# Revit family: 2019-SYP-ALTAIR-120-RE-EN
name_source: partatom
category: Mechanical Equipment
units: mm (PartAtom-declared; Revit-internal decimal feet)

## family parameters
Always vertical = Yes
Cut with Voids When Loaded = No
OmniClass Number = 23.75.00.00
OmniClass Title = Climate Control (HVAC)
Part Type = Normal
Room Calculation Point = No
Round Connector Dimension = Use Radius
Shared = No
Work Plane-Based = No

## types (1)
- default
    Air Terminal Velocity Pressure = 0.0 Pa
    AtmosphericAcidification = 0
    AtmosphericAcidificationPerUnit = 0
    BIMElementVersion = 1.0
    ClimateChange = 0
    ClimateChangePerUnit = 0
    Connector Radius 1 = 47 mm  [stored 0.154199 ft]
    Connector Radius 2 = 47 mm  [stored 0.154199 ft]
    Dimension 1 = Yes
    Dimension 2 = No
    DischargePressureLoss = 0.0 Pa
    DischargeVelocity = 0.0 m/s
    DrivePowerLoss = 0 W
    Electrical Connector Material = Plastic, Formed white
    Eutrophication = 0
    EutrophicationPerUnit = 0
    FanPowerRate = 0 W
    GrossWeight = 0.00 kg
    HasProtectiveEarth = Yes
    HazardousWaste = 0
    HazardousWastePerUnit = 0
    IFCClassification = Fans
    ImpellerDiameter = 0 mm  [stored 0 ft]
    InertWaste = 0
    InertWastePerUnit = 0
    IsExtendedWarranty = No
    MaintenanceCost = 0
    MasterformatCode = 23 00 00
    MasterformatTitle = Heating, Ventilating, and Air Conditioning (HVAC)
    MaterialHousing = Steel, Galvanized painted white
    MaterialHousing B = Steel, Galvanized painted black
    MaterialHousing C = Plastic, Formed Black
    NominalAirFlowRate = 0.0 L/s
    NominalFrequencyRange = 0 Hz
    NominalPowerRate = 0 W
    NominalStaticPressure = 0.0 Pa
    NominalTotalPressure = 0.0 Pa
    NonHazardousWaste = 0
    NonHazardousWastePerUnit = 0
    NonRenewableEnergyConsumption = 0
    NonRenewableEnergyConsumptionPerUnit = 0
    NumberOfPoles = 1
    OmniclassCode = 23-33 31 19
    OmniclassTitle = Fans
    PA = 77 mm  [stored 0.252625 ft]
    PB = 360 mm  [stored 1.1811 ft]
    PC = 550 mm
    PCUT_INT = 84 mm  [stored 0.275591 ft]
    PCUT_INT2 = 84 mm  [stored 0.275591 ft]
    PD = 94 mm  [stored 0.308399 ft]
    PE = 30 mm  [stored 0.0984252 ft]
    PF = 660 mm  [stored 2.16535 ft]
    PG = 850 mm  [stored 2.78871 ft]
    PH = 30 mm  [stored 0.0984252 ft]
    PII = 170 mm  [stored 0.557743 ft]
    PJ = 78 mm  [stored 0.255906 ft]
    PhotochemicalOzoneFormation = 0
    PhotochemicalOzoneFormationPerUnit = 0
    PowerFactor = 0.00%
    RadioactiveWaste = 0
    RadioactiveWastePerUnit = 0
    RatedCurrent = 0 A
    RatedVoltage = 0 V
    RenewableEnergyConsumption = 0
    RenewableEnergyConsumptionPerUnit = 0
    ResourceDepletion = 0
    ResourceDepletionPerUnit = 0
    ShaftPowerRate = 0 W
    StratosphericOzoneLayerDestruction = 0
    StratosphericOzoneLayerDestructionPerUnit = 0
    Support Bracket Material = Steel, Galvanized
    Throw Distance High Velocity = 0 mm  [stored 0 ft]
    Throw Distance Low Velocity = 0 mm  [stored 0 ft]
    TotalPrimaryEnergyConsumption = 0
    TotalPrimaryEnergyConsumptionPerUnit = 0
    Type Image = <None>
    UNSPSCCode = 40101604
    UNSPSCTitle = Fans
    WaterConsumption = 0
    WaterConsumptionPerUnit = 0
    spDI1 = 94 mm  [stored 0.308399 ft]
    spDO1 = 94 mm  [stored 0.308399 ft]
    spElectricalPower_Solution = 0 W
    spFanSize = 0 mm  [stored 0 ft]
    spMaxAbsorbedCurrent = 0 A
    spShaftPower_Solution = 0 W

note: [stored X ft] marks values corroborated as IEEE doubles in the binary element streams (Revit-internal decimal feet)
